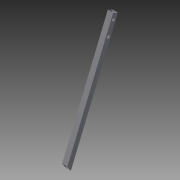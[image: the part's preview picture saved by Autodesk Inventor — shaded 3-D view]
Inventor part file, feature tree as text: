
AUTODESK INVENTOR PART (.ipt)
format: ipt  version: 2013 (Build 170138000, 138)  size: 105,984 bytes
history: native  units: in
note: dims shown in document units (in); Inventor stores cm internally (conversion verified against a paired STEP export)
features: extrude x3, sketch x3
ambient origin geometry x8: Origin, YZ Plane, XZ Plane, XY Plane, X Axis, Y Axis, Z Axis, Center Point
feature tree (6):
  extrude  "Extrusion3"  TaperAngle=90.0deg  [1 undecoded]
  extrude  "Extrusion4"  TaperAngle=22.5deg  [1 undecoded]
  extrude  "Extrusion5"  TaperAngle=180.0deg  [1 undecoded]
  sketch  "Sketch1"  dims[d0=10.0in d1=90.0deg]
  sketch  "Sketch3"  dims[d2=22.5in d3=22.5deg]
  sketch  "Sketch4"  dims[d4=1.0in d5=180.0deg d6=1.0in d7=112.5deg d8=90.0deg d17=1.0in d18=0.0in d19=0.0625in d20=0.0625in d21=0.0625in d22=0.0625in d23=100.0in d24=0.0in d25=1.0in d26=112.5deg d27=0.5in d28=2.5in d29=0.56in d30=2.0in d31=0.0in]
note: 3 required parameter values undecoded (feature->parameter linkage not recoverable at this tier; creation-order binding heuristic only, values carry confidence <= 0.55)
